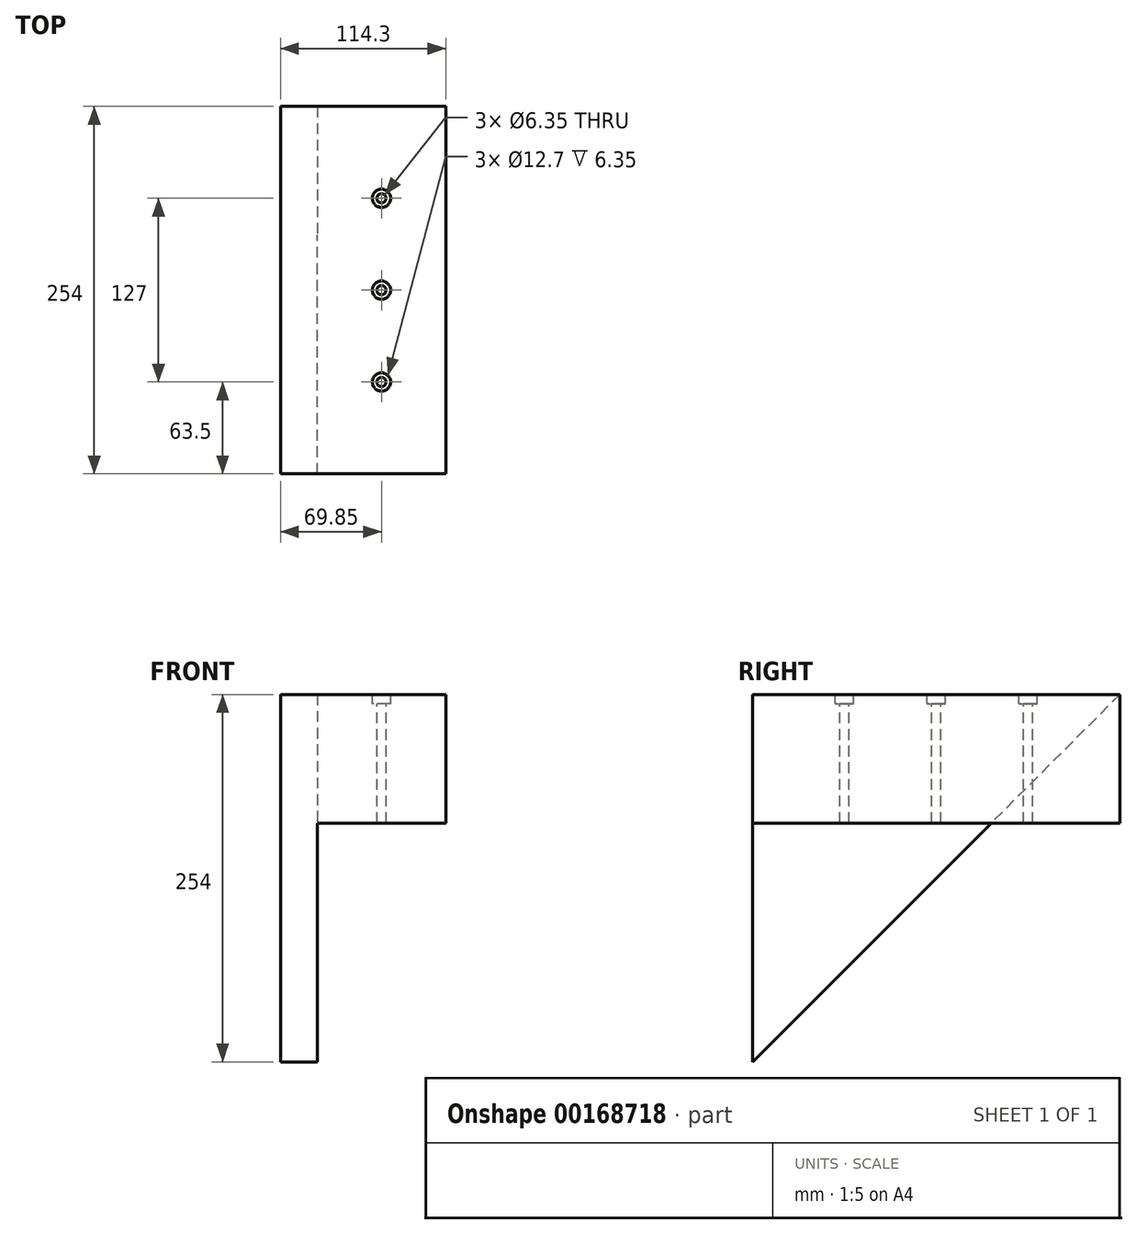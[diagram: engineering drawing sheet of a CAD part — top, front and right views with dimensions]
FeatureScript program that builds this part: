
annotation { "Feature Type Name" : "Feature", "Feature Type Description" : "" }
export const myFeature = defineFeature(function(context is Context, id is Id, definition is map)
    precondition{}
    {
        {
            var Q0;
            Q0=qCreatedBy(makeId("Front.planeOp"),FACE);
            var sketch = newSketch(context, id + "F0", { "sketchPlane" : qUnion([Q0])});
            skLineSegment(sketch, "E0.bottom", {"start": v(-44.45, 44.45) * mm, "end": v(44.45, 44.45) * mm});
            skLineSegment(sketch, "E0.top", {"start": v(-44.45, -44.45) * mm, "end": v(44.45, -44.45) * mm});
            skLineSegment(sketch, "E0.left", {"start": v(-44.45, 44.45) * mm, "end": v(-44.45, -44.45) * mm});
            skLineSegment(sketch, "E0.right", {"start": v(44.45, 44.45) * mm, "end": v(44.45, -44.45) * mm});
            skPoint(sketch, "E0.middle", {"position": v(0, 0) * mm});
            skSolve(sketch);
        }
        {
            var Q0;
            Q0=makeQuery(id+"F0.imprint","IMPRINT",FACE,{"disambiguationData":[TD([[makeQuery(id+"F0.imprint","IMPRINT",EDGE,{"derivedFrom":sQuery(id+"F0.wireOp",EDGE,"E0.bottom")}),-1.0]])]});
            extrude(context, id + "F1", {"entities" : qUnion([Q0]), "endBound" : BoundingType.SYMMETRIC, "depth" : 254 * mm});
        }
        {
            var Q0;
            Q0=makeQuery(id+"F1.opExtrude","SWEPT_FACE",FACE,{"disambiguationData":[OSD([sQuery(id+"F0.wireOp",EDGE,"E0.bottom")])]});
            var sketch = newSketch(context, id + "F2", { "sketchPlane" : qUnion([Q0])});
            skLineSegment(sketch, "E1", {"start": v(0, 127) * mm, "end": v(0, -127) * mm, "construction": true});
            skPoint(sketch, "E2", {"position": v(0, 0) * mm});
            skPoint(sketch, "E3", {"position": v(0, 63.5) * mm});
            skLineSegment(sketch, "E4", {"start": v(-44.45, 0) * mm, "end": v(44.45, 0) * mm, "construction": true});
            skPoint(sketch, "E5.MirrorP", {"position": v(0, -63.5) * mm});
            skSolve(sketch);
        }
        {
            var Q0;
            Q0=sQuery(id+"F2.wireOp",VERTEX,"E3");
            var Q1;
            Q1=sQuery(id+"F2.wireOp",VERTEX,"E2");
            var Q2;
            Q2=sQuery(id+"F2.wireOp",VERTEX,"E5.MirrorP");
            var Q3;
            Q3=makeQuery(id+"F1.opExtrude","SWEPT_BODY",BODY,{"disambiguationData":[OSD([sQuery(id+"F0.wireOp",EDGE,"E0.bottom"),sQuery(id+"F0.wireOp",EDGE,"E0.top"),sQuery(id+"F0.wireOp",EDGE,"E0.left"),sQuery(id+"F0.wireOp",EDGE,"E0.right")])]});
            hole(context, id + "F3", {"style" : HoleStyle.C_BORE, "endStyle" : HoleEndStyle.THROUGH, "holeDiameter" : 6.35 * mm, "cBoreDiameter" : 12.7 * mm, "cBoreDepth" : 6.35 * mm, "startFromSketch" : true, "locations" : qUnion([Q0, Q1, Q2]), "scope" : qUnion([Q3]), "isTappedThrough" : true});
        }
        {
            var Q0;
            Q0=makeQuery(id+"F1.opExtrude","SWEPT_FACE",FACE,{"disambiguationData":[OSD([sQuery(id+"F0.wireOp",EDGE,"E0.left")])]});
            var sketch = newSketch(context, id + "F4", { "sketchPlane" : qUnion([Q0])});
            skLineSegment(sketch, "E6.bottom", {"start": v(127, 44.45) * mm, "end": v(88.02, 44.45) * mm});
            skLineSegment(sketch, "E6.top", {"start": v(127, 0) * mm, "end": v(88.02, 0) * mm});
            skLineSegment(sketch, "E6.left", {"start": v(127, 44.45) * mm, "end": v(127, 0) * mm});
            skLineSegment(sketch, "E6.right", {"start": v(88.02, 44.45) * mm, "end": v(88.02, 0) * mm, "construction": true});
            skSolve(sketch);
        }
        {
            var Q0;
            {var subQ4=sQuery(id+"F4.wireOp",EDGE,"E6.bottom");Q0=makeQuery(id+"F4.imprint","IMPRINT",FACE,{"disambiguationData":[TD([[makeQuery(id+"F4.imprint","IMPRINT",EDGE,{"derivedFrom":subQ4}),1.0]])]});}
            var sketch = newSketch(context, id + "F5", { "sketchPlane" : qUnion([Q0])});
            skLineSegment(sketch, "E7", {"start": v(-127, 44.45) * mm, "end": v(127, -209.55) * mm});
            skLineSegment(sketch, "E8", {"start": v(127, -209.55) * mm, "end": v(127, 44.45) * mm});
            skLineSegment(sketch, "E9", {"start": v(127, 44.45) * mm, "end": v(-127, 44.45) * mm});
            skSolve(sketch);
        }
        {
            var Q0;
            Q0 = qSketchRegion(id + "F5", true);
            extrude(context, id + "F6", {"entities" : qUnion([Q0]), "operationType" : NewBodyOperationType.ADD, "depth" : 25.4 * mm, "offsetDistance" : 25.4 * mm});
        }
    });
